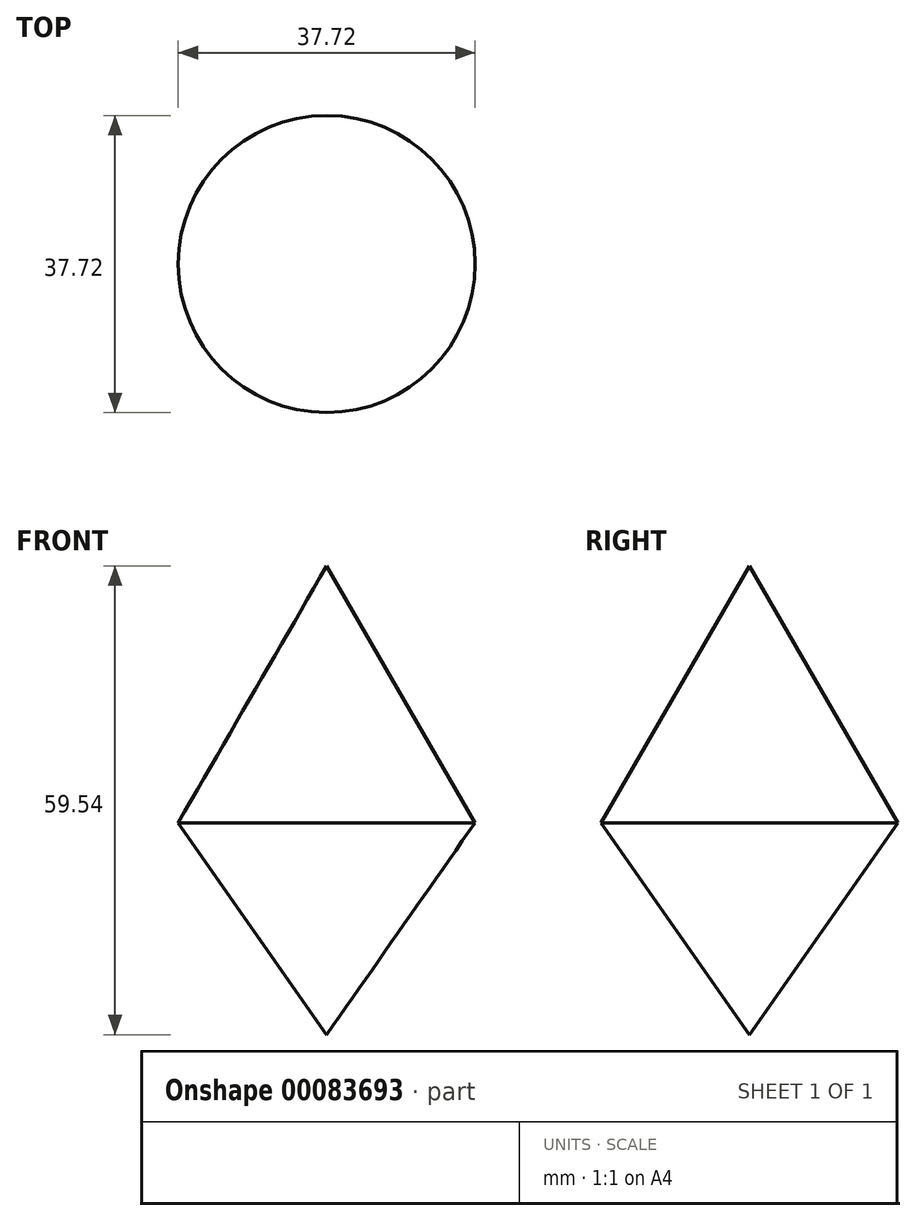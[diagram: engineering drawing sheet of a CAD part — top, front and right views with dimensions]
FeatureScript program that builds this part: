
annotation { "Feature Type Name" : "Feature", "Feature Type Description" : "" }
export const myFeature = defineFeature(function(context is Context, id is Id, definition is map)
    precondition{}
    {
        {
            var Q0;
            Q0=qCreatedBy(makeId("Front.planeOp"),FACE);
            var sketch = newSketch(context, id + "F0", { "sketchPlane" : qUnion([Q0])});
            skLineSegment(sketch, "E0", {"start": v(0, 32.61) * mm, "end": v(-18.86, 0) * mm});
            skLineSegment(sketch, "E1", {"start": v(-18.86, 0) * mm, "end": v(0, -26.93) * mm});
            skLineSegment(sketch, "E2", {"start": v(0, -26.93) * mm, "end": v(0, 32.61) * mm});
            skSolve(sketch);
        }
        {
            var Q0;
            Q0=makeQuery(id+"F0.imprint","IMPRINT",FACE,{"disambiguationData":[TD([[makeQuery(id+"F0.imprint","IMPRINT",EDGE,{"derivedFrom":sQuery(id+"F0.wireOp",EDGE,"E0")}),1.0]])]});
            var Q1;
            Q1=sQuery(id+"F0.wireOp",EDGE,"E2");
            revolve(context, id + "F1", {"entities" : qUnion([Q0]), "axis" : qUnion([Q1]), "revolveType" : RevolveType.FULL});
        }
    });
